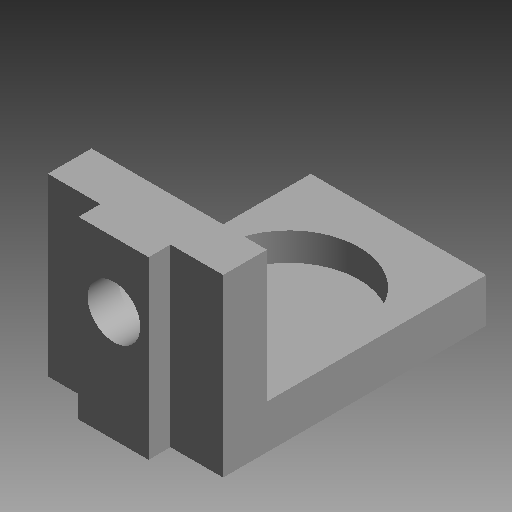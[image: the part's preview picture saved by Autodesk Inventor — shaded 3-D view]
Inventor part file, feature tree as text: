
AUTODESK INVENTOR PART (.ipt)
format: ipt  version: 2019 (Build 230136000, 136)  size: 99,840 bytes
history: native  units: mm (DEFAULTED — no unit token found)
features: sketch x4, other x3
ambient origin geometry x8: Origin, YZ Plane, XZ Plane, XY Plane, X Axis, Y Axis, Z Axis, Center Point
bodies: Solid1 (feature_tree)
feature tree (7):
  other  "spring tab for on arm"
  other  "Solid1::spring tab for on arm"
  other  "TaggingFeature1"
  sketch  "Sketch1"  dims[d0=10.0mm]
  sketch  "Sketch3"
  sketch  "Sketch4"
  sketch  "Sketch5"
